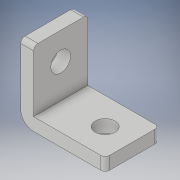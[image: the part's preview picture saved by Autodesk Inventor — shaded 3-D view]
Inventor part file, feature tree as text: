
AUTODESK INVENTOR PART (.ipt)
format: ipt  version: 2017 (Build 210142000, 142)  size: 133,632 bytes
history: native  units: in
note: dims shown in document units (in); Inventor stores cm internally (conversion verified against a paired STEP export)
features: extrude x3, sketch x3, fillet x1
ambient origin geometry x8: Origin, YZ Plane, XZ Plane, XY Plane, X Axis, Y Axis, Z Axis, Center Point
bodies: Body1 (feature_tree)
feature tree (7):
  extrude  "Extrusion2"  Depth=0.285in
  fillet  "Fillet2"  Radius=0.333in
  extrude  "Extrusion3"  Depth=0.02in
  extrude  "Extrusion4"  Depth=0.252in
  sketch  "Sketch2"  dims[d9=0.06in d10=0.285in d11=0.333in]
  sketch  "Sketch3"  dims[d12=0.252in d13=0.0in d14=0.02in]
  sketch  "Sketch4"  dims[d15=0.126in d16=0.126in d17=0.092in d18=0.252in d19=0.0in d20=0.126in d21=0.126in d22=0.092in d23=0.252in d24=0.0in]
